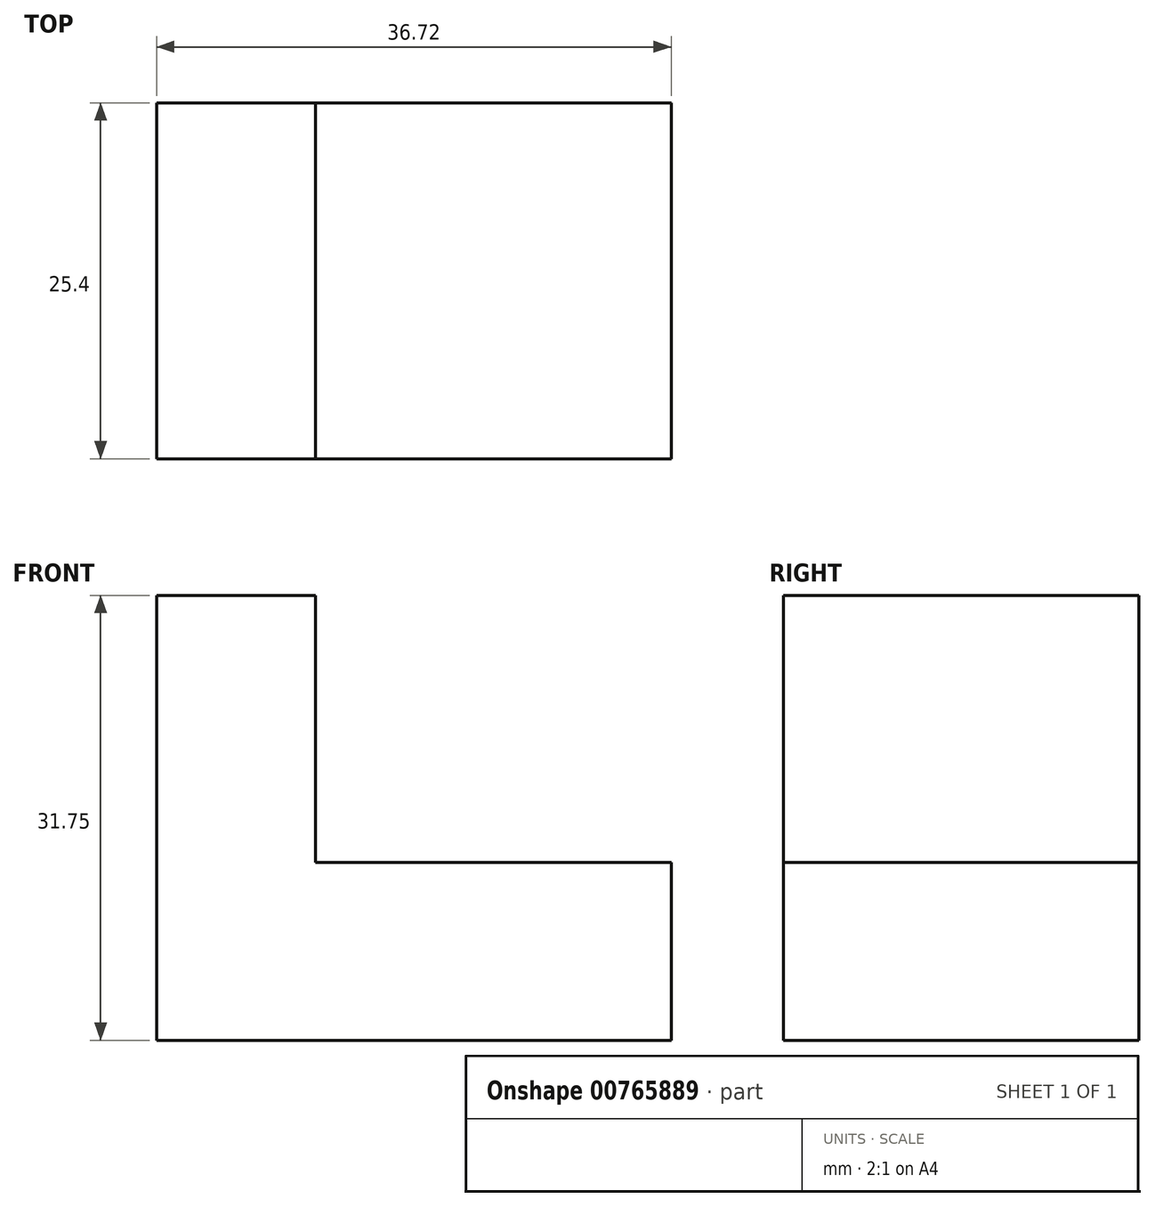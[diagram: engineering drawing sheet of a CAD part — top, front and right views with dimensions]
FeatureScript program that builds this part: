
annotation { "Feature Type Name" : "Feature", "Feature Type Description" : "" }
export const myFeature = defineFeature(function(context is Context, id is Id, definition is map)
    precondition{}
    {
        {
            var Q0;
            Q0=qCreatedBy(makeId("Front.planeOp"),FACE);
            var sketch = newSketch(context, id + "F0", { "sketchPlane" : qUnion([Q0])});
            skLineSegment(sketch, "E0", {"start": v(0, 0) * mm, "end": v(36.72, 0) * mm});
            skLineSegment(sketch, "E1", {"start": v(36.72, 0) * mm, "end": v(36.72, 12.7) * mm});
            skLineSegment(sketch, "E2", {"start": v(11.32, 12.7) * mm, "end": v(36.72, 12.7) * mm});
            skLineSegment(sketch, "E3", {"start": v(11.32, 12.7) * mm, "end": v(11.32, 31.75) * mm});
            skLineSegment(sketch, "E4", {"start": v(11.32, 31.75) * mm, "end": v(0, 31.75) * mm});
            skLineSegment(sketch, "E5", {"start": v(0, 31.75) * mm, "end": v(0, 0) * mm});
            skSolve(sketch);
        }
        {
            var Q0;
            Q0 = qSketchRegion(id + "F0", true);
            extrude(context, id + "F1", {"entities" : qUnion([Q0]), "depth" : 25.4 * mm, "offsetDistance" : 25.4 * mm});
        }
    });
